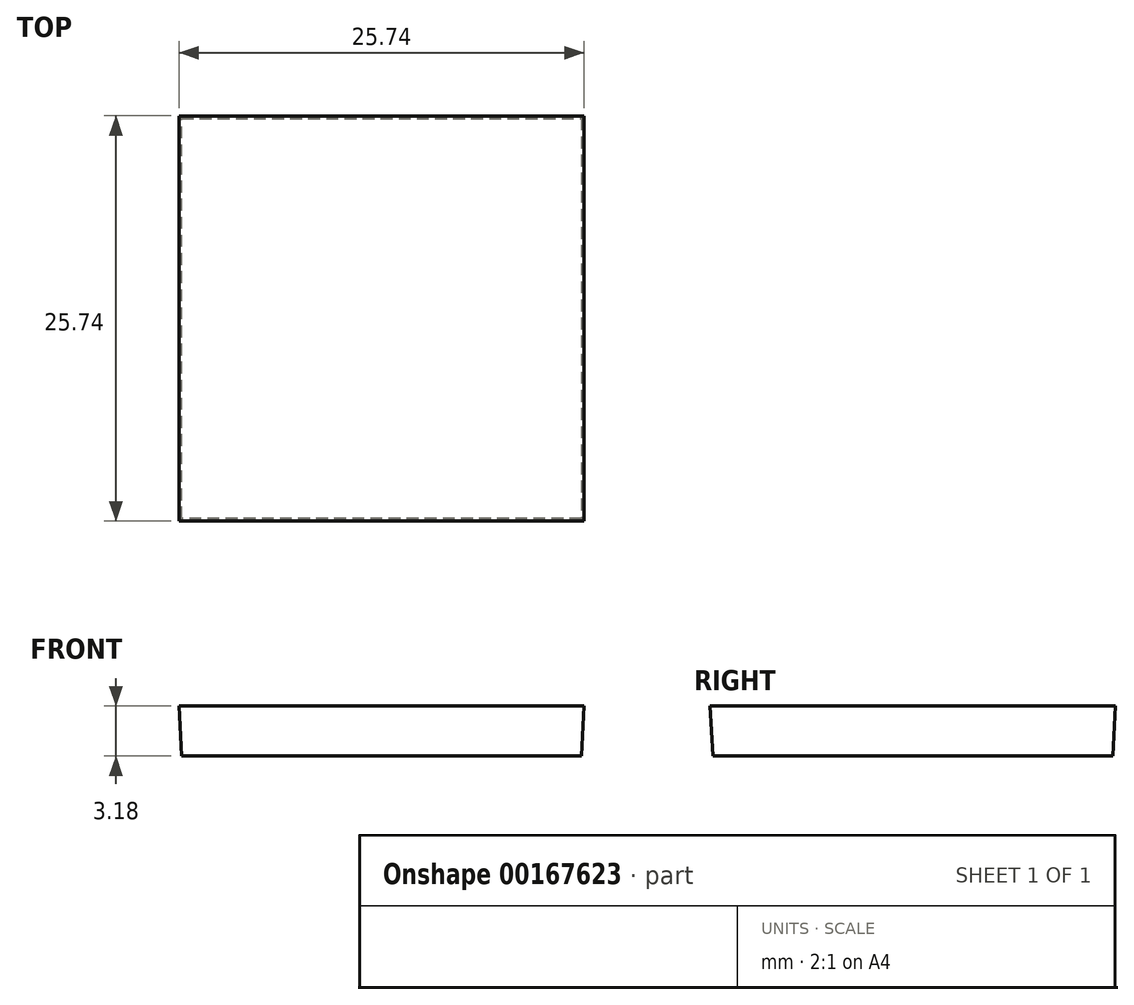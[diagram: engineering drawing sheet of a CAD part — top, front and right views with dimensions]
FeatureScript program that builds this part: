
annotation { "Feature Type Name" : "Feature", "Feature Type Description" : "" }
export const myFeature = defineFeature(function(context is Context, id is Id, definition is map)
    precondition{}
    {
        {
            var Q0;
            Q0=qCreatedBy(makeId("Top.planeOp"),FACE);
            var sketch = newSketch(context, id + "F0", { "sketchPlane" : qUnion([Q0])});
            skLineSegment(sketch, "E0.bottom", {"start": v(12.7, 12.7) * mm, "end": v(-12.7, 12.7) * mm});
            skLineSegment(sketch, "E0.top", {"start": v(12.7, -12.7) * mm, "end": v(-12.7, -12.7) * mm});
            skLineSegment(sketch, "E0.left", {"start": v(12.7, 12.7) * mm, "end": v(12.7, -12.7) * mm});
            skLineSegment(sketch, "E0.right", {"start": v(-12.7, 12.7) * mm, "end": v(-12.7, -12.7) * mm});
            skPoint(sketch, "E0.middle", {"position": v(0, 0) * mm});
            skSolve(sketch);
        }
        {
            var Q0;
            Q0 = qSketchRegion(id + "F0", true);
            extrude(context, id + "F1", {"entities" : qUnion([Q0]), "depth" : 3.17 * mm, "hasDraft" : true, "draftAngle" : 3 * degree});
        }
    });
